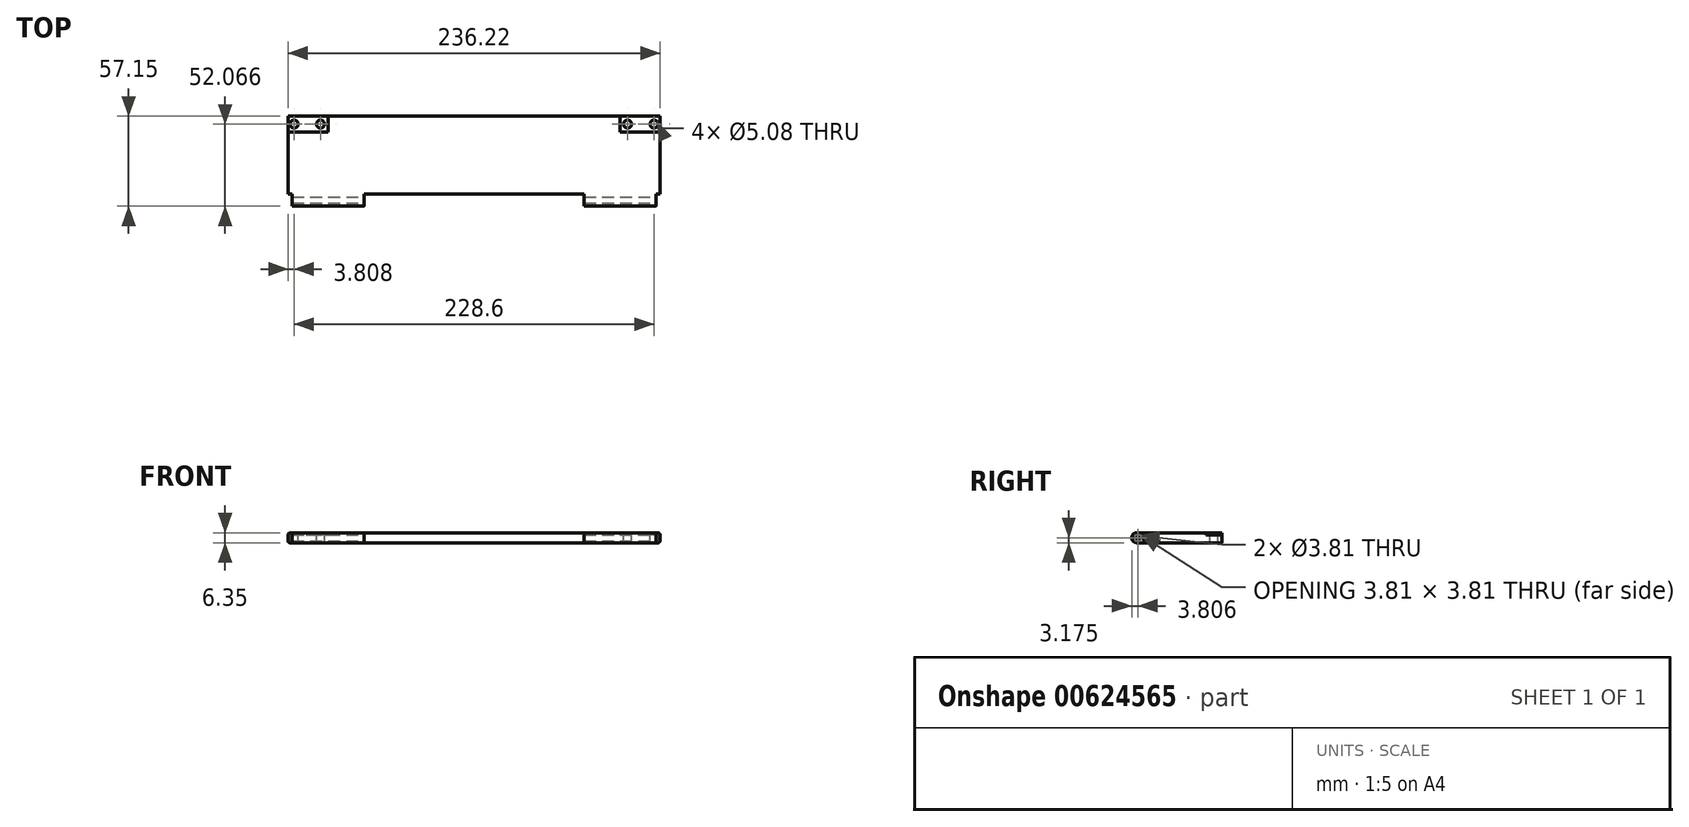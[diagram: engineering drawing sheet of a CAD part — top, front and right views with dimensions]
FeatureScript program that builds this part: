
annotation { "Feature Type Name" : "Feature", "Feature Type Description" : "" }
export const myFeature = defineFeature(function(context is Context, id is Id, definition is map)
    precondition{}
    {
        {
            var Q0;
            Q0=qCreatedBy(makeId("Top.planeOp"),FACE);
            var sketch = newSketch(context, id + "F0", { "sketchPlane" : qUnion([Q0])});
            skLineSegment(sketch, "E0.bottom", {"start": v(-101.64, -2.08) * mm, "end": v(-53.38, -2.08) * mm});
            skLineSegment(sketch, "E0.left", {"start": v(-101.64, -2.08) * mm, "end": v(-101.64, -51.61) * mm});
            skLineSegment(sketch, "E0.right", {"start": v(134.58, -2.08) * mm, "end": v(134.58, -51.61) * mm});
            skLineSegment(sketch, "E1.left", {"start": v(-53.38, -51.61) * mm, "end": v(-53.38, -59.23) * mm});
            skPoint(sketch, "E2.oppositeSnap0", {"position": v(86.32, -66.98) * mm});
            skLineSegment(sketch, "E2.top", {"start": v(-53.38, -2.08) * mm, "end": v(86.32, -2.08) * mm});
            skLineSegment(sketch, "E2.left", {"start": v(-53.38, -2.08) * mm, "end": v(-53.38, -2.08) * mm});
            skLineSegment(sketch, "E2.right", {"start": v(86.32, -2.08) * mm, "end": v(86.32, -2.08) * mm});
            skLineSegment(sketch, "E3.trimOffspring", {"start": v(86.32, -2.08) * mm, "end": v(134.58, -2.08) * mm});
            skLineSegment(sketch, "E4.top", {"start": v(-101.64, -59.23) * mm, "end": v(-53.38, -59.23) * mm});
            skLineSegment(sketch, "E4.left", {"start": v(-101.64, -51.61) * mm, "end": v(-101.64, -59.23) * mm});
            skLineSegment(sketch, "E5.bottom", {"start": v(86.32, -59.23) * mm, "end": v(134.58, -59.23) * mm});
            skLineSegment(sketch, "E5.right", {"start": v(134.58, -59.23) * mm, "end": v(134.58, -51.61) * mm});
            skLineSegment(sketch, "E6", {"start": v(-53.38, -51.61) * mm, "end": v(86.32, -51.61) * mm});
            skLineSegment(sketch, "E7", {"start": v(86.32, -59.23) * mm, "end": v(86.32, -51.61) * mm});
            skSolve(sketch);
        }
        {
            var Q0;
            Q0=qSketchRegion(id+"F0",true);
            extrude(context, id + "F1", {"entities" : qUnion([Q0]), "depth" : 6.35 * mm});
        }
        {
            var Q0;
            Q0=makeQuery(id+"F1.opExtrude","CAP_FACE",FACE,{"disambiguationData":[OSD([sQuery(id+"F0.wireOp",EDGE,"E0.bottom"),sQuery(id+"F0.wireOp",EDGE,"E0.top"),sQuery(id+"F0.wireOp",EDGE,"E0.left"),sQuery(id+"F0.wireOp",EDGE,"E0.right"),sQuery(id+"F0.wireOp",EDGE,"E1.top"),sQuery(id+"F0.wireOp",EDGE,"E1.left"),sQuery(id+"F0.wireOp",EDGE,"E1.right"),sQuery(id+"F0.wireOp",EDGE,"E2.top"),sQuery(id+"F0.wireOp",EDGE,"E3.trimOffspring"),sQuery(id+"F0.wireOp",EDGE,"966923a9-03d6-48e2-8a9f-226ebbd281b2.trimOffspring")])],"isStart":false});
            var sketch = newSketch(context, id + "F2", { "sketchPlane" : qUnion([Q0])});
            skLineSegment(sketch, "E8.bottom", {"start": v(-101.64, -2.08) * mm, "end": v(-76.24, -2.08) * mm});
            skLineSegment(sketch, "E8.top", {"start": v(-101.64, -12.24) * mm, "end": v(-76.24, -12.24) * mm});
            skLineSegment(sketch, "E8.left", {"start": v(-101.64, -2.08) * mm, "end": v(-101.64, -12.24) * mm});
            skLineSegment(sketch, "E8.right", {"start": v(-76.24, -2.08) * mm, "end": v(-76.24, -12.24) * mm});
            skLineSegment(sketch, "E9.bottom", {"start": v(134.58, -2.08) * mm, "end": v(109.18, -2.08) * mm});
            skLineSegment(sketch, "E9.top", {"start": v(134.58, -12.24) * mm, "end": v(109.18, -12.24) * mm});
            skLineSegment(sketch, "E9.left", {"start": v(134.58, -2.08) * mm, "end": v(134.58, -12.24) * mm});
            skLineSegment(sketch, "E9.right", {"start": v(109.18, -2.08) * mm, "end": v(109.18, -12.24) * mm});
            skSolve(sketch);
        }
        {
            var Q0;
            Q0=qSketchRegion(id+"F2",true);
            extrude(context, id + "F3", {"entities" : qUnion([Q0]), "operationType" : NewBodyOperationType.REMOVE, "oppositeDirection" : true, "depth" : 1.27 * mm});
        }
        {
            var Q0;
            Q0=makeQuery(id+"F3.boolean.opBoolean","COPY",FACE,{"derivedFrom":makeQuery(id+"F3.opExtrude","CAP_FACE",FACE,{"disambiguationData":[OSD([sQuery(id+"F2.wireOp",EDGE,"E8.bottom"),sQuery(id+"F2.wireOp",EDGE,"E8.top"),sQuery(id+"F2.wireOp",EDGE,"E8.left"),sQuery(id+"F2.wireOp",EDGE,"E8.right")])],"isStart":false})});
            var sketch = newSketch(context, id + "F4", { "sketchPlane" : qUnion([Q0])});
            skCircle(sketch, "E10", {"center": v(-97.83, -7.16) * mm, "radius": 2.54 * mm});
            skPoint(sketch, "E10.centerSnap0", {"position": v(-101.64, -7.16) * mm});
            skCircle(sketch, "E11", {"center": v(-81.07, -7.16) * mm, "radius": 2.54 * mm});
            skSolve(sketch);
        }
        {
            var Q0;
            Q0=qSketchRegion(id+"F4",true);
            extrude(context, id + "F5", {"entities" : qUnion([Q0]), "operationType" : NewBodyOperationType.REMOVE, "oppositeDirection" : true, "depth" : 25.4 * mm});
        }
        {
            var Q0;
            Q0=makeQuery(id+"F3.boolean.opBoolean","COPY",FACE,{"derivedFrom":makeQuery(id+"F3.opExtrude","CAP_FACE",FACE,{"disambiguationData":[OSD([sQuery(id+"F2.wireOp",EDGE,"E9.bottom"),sQuery(id+"F2.wireOp",EDGE,"E9.top"),sQuery(id+"F2.wireOp",EDGE,"E9.left"),sQuery(id+"F2.wireOp",EDGE,"E9.right")])],"isStart":false})});
            var sketch = newSketch(context, id + "F6", { "sketchPlane" : qUnion([Q0])});
            skCircle(sketch, "E12", {"center": v(130.77, -7.16) * mm, "radius": 2.54 * mm});
            skPoint(sketch, "E12.centerSnap0", {"position": v(134.58, -7.16) * mm});
            skCircle(sketch, "E13", {"center": v(114, -7.16) * mm, "radius": 2.54 * mm});
            skSolve(sketch);
        }
        {
            var Q0;
            Q0=qSketchRegion(id+"F6",true);
            extrude(context, id + "F7", {"entities" : qUnion([Q0]), "operationType" : NewBodyOperationType.REMOVE, "oppositeDirection" : true, "depth" : 25.4 * mm});
        }
        {
            var Q0;
            Q0=makeQuery(id+"F1.opExtrude","SWEPT_FACE",FACE,{"disambiguationData":[OSD([sQuery(id+"F0.wireOp",EDGE,"E1.left")])]});
            var sketch = newSketch(context, id + "F8", { "sketchPlane" : qUnion([Q0])});
            skCircle(sketch, "E14", {"center": v(-55.42, 3.18) * mm, "radius": 1.9 * mm});
            skPoint(sketch, "E14.centerSnap0", {"position": v(-55.42, 6.35) * mm});
            skPoint(sketch, "E14.centerSnap1", {"position": v(-59.23, 3.18) * mm});
            skSolve(sketch);
        }
        {
            var Q0;
            Q0=qSketchRegion(id+"F8",true);
            extrude(context, id + "F9", {"entities" : qUnion([Q0]), "operationType" : NewBodyOperationType.REMOVE, "endBound" : BoundingType.SYMMETRIC, "oppositeDirection" : true, "depth" : 508 * mm});
        }
        {
            var Q0;
            Q0=makeQuery(id+"F1.opExtrude","CAP_EDGE",EDGE,{"disambiguationData":[OSD([sQuery(id+"F0.wireOp",EDGE,"E4.top")])],"isStart":false});
            var Q1;
            Q1=makeQuery(id+"F1.opExtrude","CAP_EDGE",EDGE,{"disambiguationData":[OSD([sQuery(id+"F0.wireOp",EDGE,"E4.top")])],"isStart":true});
            var Q2;
            Q2=makeQuery(id+"F1.opExtrude","CAP_EDGE",EDGE,{"disambiguationData":[OSD([sQuery(id+"F0.wireOp",EDGE,"E5.bottom")])],"isStart":false});
            var Q3;
            Q3=makeQuery(id+"F1.opExtrude","CAP_EDGE",EDGE,{"disambiguationData":[OSD([sQuery(id+"F0.wireOp",EDGE,"E5.bottom")])],"isStart":true});
            fillet(context, id + "F10", {"entities" : qUnion([Q0, Q1, Q2, Q3]), "radius" : 3.17 * mm, "tangentPropagation" : true, "allowEdgeOverflow" : false});
        }
        {
            var Q0;
            Q0=makeQuery(id+"F1.opExtrude","CAP_EDGE",EDGE,{"disambiguationData":[OSD([sQuery(id+"F0.wireOp",EDGE,"E0.left"),sQuery(id+"F0.wireOp",EDGE,"E4.left")])],"isStart":false});
            var Q1;
            Q1=makeQuery(id+"F1.opExtrude","CAP_EDGE",EDGE,{"disambiguationData":[OSD([sQuery(id+"F0.wireOp",EDGE,"E0.right"),sQuery(id+"F0.wireOp",EDGE,"E5.right")])],"isStart":false});
            fillet(context, id + "F11", {"entities" : qUnion([Q0, Q1]), "radius" : 1.27 * mm, "tangentPropagation" : true, "allowEdgeOverflow" : false});
        }
        {
            var Q0;
            Q0=makeQuery(id+"F11.opFillet","SPLIT",FACE,{"disambiguationData":[OD(0.0)],"derivedFrom":makeQuery(id+"F1.opExtrude","SWEPT_FACE",FACE,{"disambiguationData":[OSD([sQuery(id+"F0.wireOp",EDGE,"E0.left"),sQuery(id+"F0.wireOp",EDGE,"E4.left")])]})});
            var sketch = newSketch(context, id + "F12", { "sketchPlane" : qUnion([Q0])});
            skLineSegment(sketch, "E15.bottom", {"start": v(51.61, 8.56) * mm, "end": v(62.33, 8.56) * mm});
            skLineSegment(sketch, "E15.top", {"start": v(51.61, -2.8) * mm, "end": v(62.33, -2.8) * mm});
            skLineSegment(sketch, "E15.left", {"start": v(51.61, 8.56) * mm, "end": v(51.61, -2.8) * mm});
            skLineSegment(sketch, "E15.right", {"start": v(62.33, 8.56) * mm, "end": v(62.33, -2.8) * mm});
            skSolve(sketch);
        }
        {
            var Q0;
            Q0=qSketchRegion(id+"F12",true);
            extrude(context, id + "F13", {"entities" : qUnion([Q0]), "operationType" : NewBodyOperationType.REMOVE, "oppositeDirection" : true, "depth" : 2.54 * mm});
        }
        {
            var Q0;
            Q0=makeQuery(id+"F11.opFillet","SPLIT",FACE,{"disambiguationData":[OD(0.0)],"derivedFrom":makeQuery(id+"F1.opExtrude","SWEPT_FACE",FACE,{"disambiguationData":[OSD([sQuery(id+"F0.wireOp",EDGE,"E0.right"),sQuery(id+"F0.wireOp",EDGE,"E5.right")])]})});
            var sketch = newSketch(context, id + "F14", { "sketchPlane" : qUnion([Q0])});
            skLineSegment(sketch, "E16.bottom", {"start": v(-59.43, 6.53) * mm, "end": v(-51.61, 6.53) * mm});
            skLineSegment(sketch, "E16.top", {"start": v(-59.43, -0.54) * mm, "end": v(-51.61, -0.54) * mm});
            skLineSegment(sketch, "E16.left", {"start": v(-59.43, 6.53) * mm, "end": v(-59.43, -0.54) * mm});
            skLineSegment(sketch, "E16.right", {"start": v(-51.61, 6.53) * mm, "end": v(-51.61, -0.54) * mm});
            skSolve(sketch);
        }
        {
            var Q0;
            Q0=qSketchRegion(id+"F14",true);
            extrude(context, id + "F15", {"entities" : qUnion([Q0]), "operationType" : NewBodyOperationType.REMOVE, "oppositeDirection" : true, "depth" : 2.54 * mm});
        }
    });
